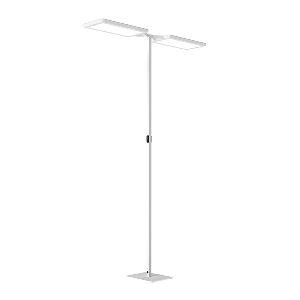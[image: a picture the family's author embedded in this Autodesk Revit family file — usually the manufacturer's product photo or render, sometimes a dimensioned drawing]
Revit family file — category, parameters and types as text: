
# Revit family: yara_doublet_-_yts_2_12000_840_r_ws_cee_00_c_114268000-00808892_17a9
name_source: partatom
category: Lighting Fixtures
units: mm (PartAtom-declared; Revit-internal decimal feet)

## family parameters
Cut with Voids When Loaded = No
Host = Face
Light Source = No
Part Type = Normal
Room Calculation Point = No
Round Connector Dimension = Use Diameter
Shared = No

## types (1)
- YARA.doubleT - YTS 2/12000/840/R/WS/CEE/00/C (1 x LED, 12000 lm, 4000K)
    Apparent Load = 168 VA
    Approval mark = CE
    CIE Flux Codes = 58 87 97 13 100
    Color Rendering = 80-89
    Color Temperature = 4000K
    Control Gear = Electronic ballast
    Default Elevation = 1800 mm
    Description = YTS 2/12000/840/R/WS/CEE/00/R|Free-standing luminaire|light source: LED|work equipment: Electronic ballast DALI|connected load: 220-240 V, 50/60 Hz|Power consumption: approx. 166 W|power factor: approx. 0,966|luminous flux: 24000 lm|luminous efficacy: 144 lm/W|light distribution: Direct/indirect|direct ratio: approx. 13 %|colour temperature: Cold white, ca. 4000 K|color rendering index (CRI): >= 80|chromaticity tolerance:  3 SDCM|technology: Presence and daylight sensor control (PIR)|operation: Wireless switch|luminaire body|material: Aluminium/plastic|surface: Powder coatet|colour: White|lamp cover: Acrylic (PMMA), Satine, Structured|tubular section|material: Steel tube|surface: Powder-coated|Form: Tubular section upright|colour of tubular section: White|luminaire base|Form: Rectangular flat|weight (net): approx. 24.0 kg|mains lead: 3.00 m Mains plug CEE 7/VII|Fastening: Floor standing base|glare control: Conical prismatic screen|luminance(L65): <= 2200 cd/m|unified glare rating(4H 8H): <=  16|special features: App control, Asymmetric radiation, Direct and indirect lighting component with edge light and light guidetechnology for a homogeneous light exit, Flicker-free, Magnetic control panel, freely positionable, PIR movement and daylight sensor|Approval mark: VDE - ENEC|
    Frequency = 50 Hz, 60 Hz
    Height = 24 mm  [stored 0.0787402 ft]
    Lamp = 1 x LED
    Lamp Light Flux = 12000 lm
    Lamp count = 1
    Length = 690 mm
    Luminous efficacy = 143 lm/W
    Manufacturer = Waldmann
    ModVariant = No
    Model = 114268000-00808892
    Mounting Place = Floor
    Mounting Type = Freestanding
    Number of Poles = 1
    OnlyDefault = Yes
    Power Factor = 1
    Product Name = YARA.doubleT - YTS 2/12000/840/R/WS/CEE/00/C
    Product group = Free standing luminaire
    ProductGroupID = 13
    Protection Class = Protection class I
    Protection Degree = IP 20
    RLX_Detail_Level = 1
    RlxData = <blob elided: 62617 chars, md5=cc444af8>
    Socket = socket
    Standby Power = 0 W
    System Light Flux = 24000 lm
    System Power = 168 W
    Type Comments = Product without accessories
    Type Image = yts-r-ws-r.jpg
    URL = http://relux.com
    VarID = ---
    Voltage = 230 V
    Voltage Range = 220-240 V
    Weight = 0.00 kg
    Width = 358 mm

note: [stored X ft] marks values corroborated as IEEE doubles in the binary element streams (Revit-internal decimal feet)

## geometry (parser evidence)
native form markers: Blend x4, Sweep x20
no freeform markers — native parametric forms only
